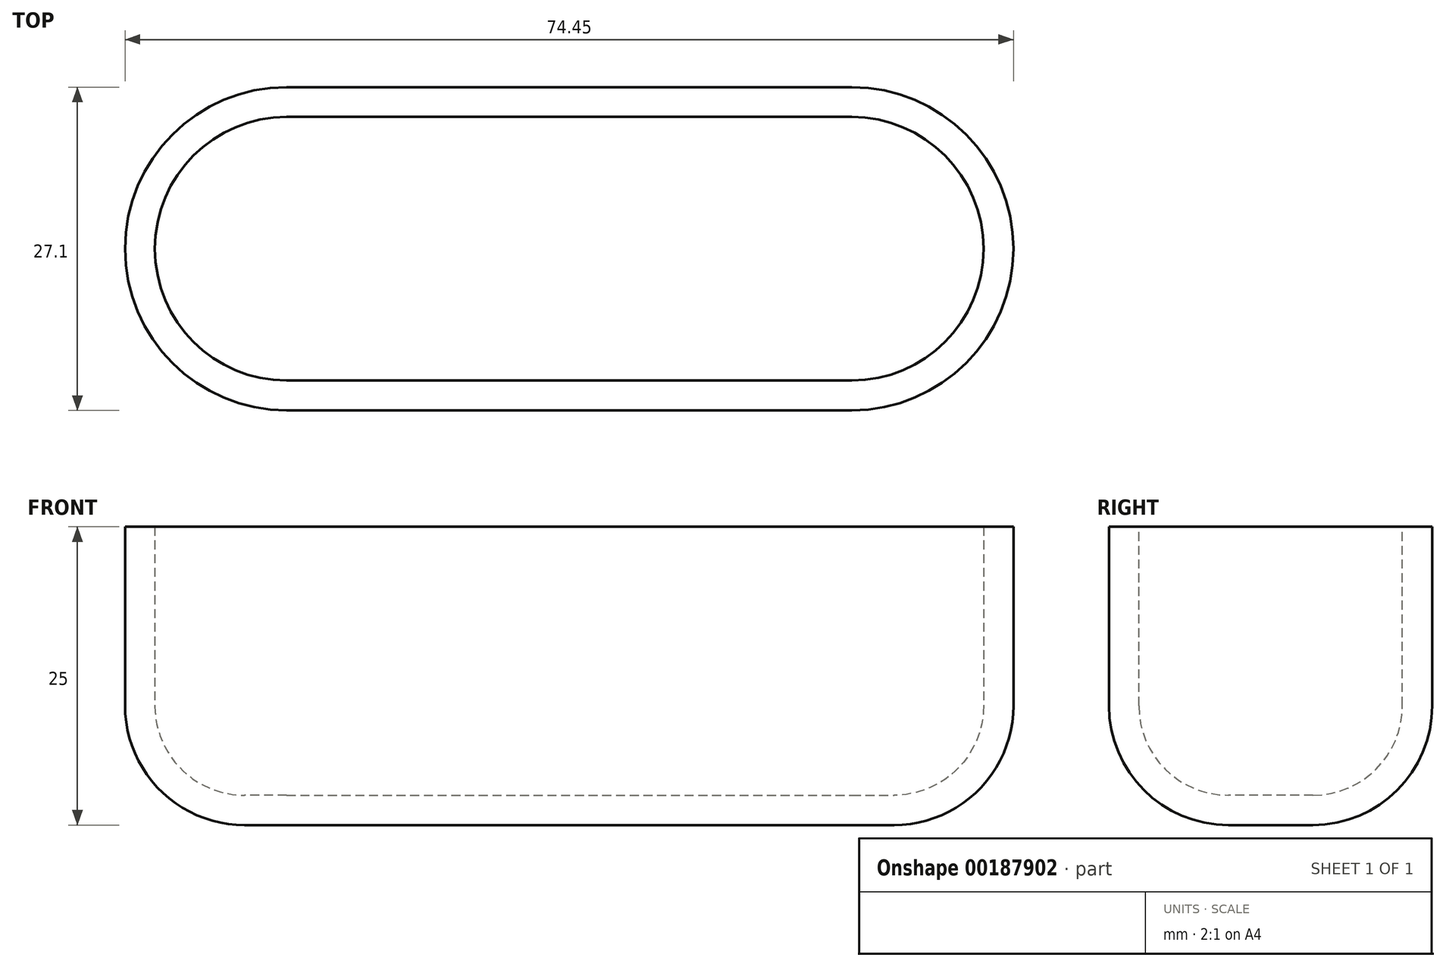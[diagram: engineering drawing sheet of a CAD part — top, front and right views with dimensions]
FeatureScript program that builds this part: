
annotation { "Feature Type Name" : "Feature", "Feature Type Description" : "" }
export const myFeature = defineFeature(function(context is Context, id is Id, definition is map)
    precondition{}
    {
        {
            var Q0;
            Q0=qCreatedBy(makeId("Top.planeOp"),FACE);
            var sketch = newSketch(context, id + "F0", { "sketchPlane" : qUnion([Q0])});
            skArc(sketch, "E0", {"start": v(0, -13.55) * mm, "mid": v(13.55, 0) * mm, "end": v(0, 13.55) * mm});
            skArc(sketch, "E1", {"start": v(-47.36, 13.55) * mm, "mid": v(-60.9, 0) * mm, "end": v(-47.36, -13.55) * mm});
            skLineSegment(sketch, "E2", {"start": v(-47.36, 13.55) * mm, "end": v(0, 13.55) * mm});
            skLineSegment(sketch, "E3", {"start": v(-47.36, -13.55) * mm, "end": v(0, -13.55) * mm});
            skSolve(sketch);
        }
        {
            var Q0;
            Q0 = qSketchRegion(id + "F0", true);
            extrude(context, id + "F1", {"entities" : qUnion([Q0]), "depth" : 25 * mm});
        }
        {
            var Q0;
            Q0 = qSketchRegion(id + "F0", true);
            extrude(context, id + "F2", {"entities" : qUnion([Q0]), "operationType" : NewBodyOperationType.ADD, "depth" : 25 * mm});
        }
        {
            var Q0;
            Q0=makeQuery(id+"F1.opExtrude","CAP_EDGE",EDGE,{"disambiguationData":[OSD([sQuery(id+"F0.wireOp",EDGE,"E1")])],"isStart":true});
            fillet(context, id + "F3", {"entities" : qUnion([Q0]), "radius" : 10 * mm, "tangentPropagation" : true, "allowEdgeOverflow" : false});
        }
        {
            var Q0;
            Q0=makeQuery(id+"F1.opExtrude","CAP_FACE",FACE,{"disambiguationData":[OSD([sQuery(id+"F0.wireOp",EDGE,"E0"),sQuery(id+"F0.wireOp",EDGE,"E1"),sQuery(id+"F0.wireOp",EDGE,"E2"),sQuery(id+"F0.wireOp",EDGE,"E3")])],"isStart":false});
            shell(context, id + "F4", {"entities" : qUnion([Q0]), "thickness" : 2.5 * mm});
        }
    });
